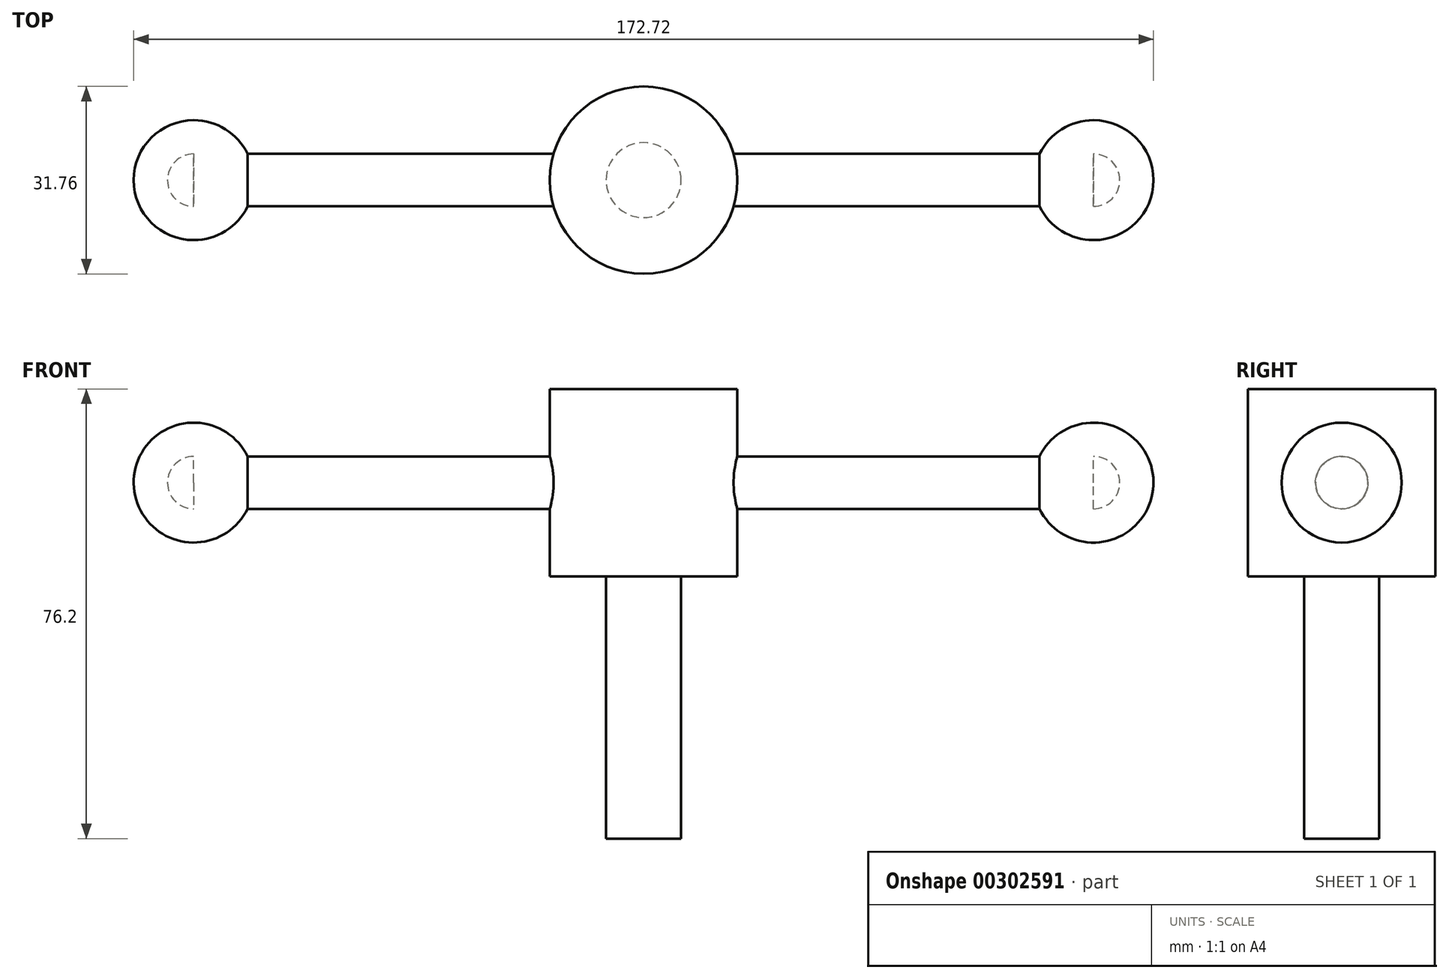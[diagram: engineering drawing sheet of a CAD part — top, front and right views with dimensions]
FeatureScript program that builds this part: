
annotation { "Feature Type Name" : "Feature", "Feature Type Description" : "" }
export const myFeature = defineFeature(function(context is Context, id is Id, definition is map)
    precondition{}
    {
        {
            var Q0;
            Q0=qCreatedBy(makeId("Top.planeOp"),FACE);
            var sketch = newSketch(context, id + "F0", { "sketchPlane" : qUnion([Q0])});
            skCircle(sketch, "E0", {"center": v(0, 0) * mm, "radius": 6.35 * mm});
            skSolve(sketch);
        }
        {
            var Q0;
            Q0 = qSketchRegion(id + "F0", true);
            extrude(context, id + "F1", {"entities" : qUnion([Q0]), "depth" : 76.2 * mm});
        }
        {
            var Q0;
            Q0=makeQuery(id+"F1.opExtrude","CAP_FACE",FACE,{"disambiguationData":[OSD([sQuery(id+"F0.wireOp",EDGE,"E0")])],"isStart":false});
            var sketch = newSketch(context, id + "F2", { "sketchPlane" : qUnion([Q0])});
            skCircle(sketch, "E1", {"center": v(0, 0) * mm, "radius": 15.88 * mm});
            skSolve(sketch);
        }
        {
            var Q0;
            Q0 = qSketchRegion(id + "F2", true);
            extrude(context, id + "F3", {"entities" : qUnion([Q0]), "operationType" : NewBodyOperationType.ADD, "oppositeDirection" : true, "depth" : 31.75 * mm});
        }
        {
            var Q0;
            Q0=qCreatedBy(makeId("Right.planeOp"),FACE);
            var sketch = newSketch(context, id + "F4", { "sketchPlane" : qUnion([Q0])});
            skLineSegment(sketch, "E2", {"start": v(0, 0) * mm, "end": v(0, 60.32) * mm});
            skCircle(sketch, "E3", {"center": v(0, 60.32) * mm, "radius": 4.45 * mm});
            skSolve(sketch);
        }
        {
            var Q0;
            Q0 = qSketchRegion(id + "F4", true);
            extrude(context, id + "F5", {"entities" : qUnion([Q0]), "operationType" : NewBodyOperationType.ADD, "endBound" : BoundingType.SYMMETRIC, "depth" : 152.4 * mm});
        }
        {
            var Q0;
            Q0=makeQuery(id+"F5.opExtrude","CAP_FACE",FACE,{"disambiguationData":[OSD([sQuery(id+"F4.wireOp",EDGE,"E3")])],"isStart":false});
            var sketch = newSketch(context, id + "F6", { "sketchPlane" : qUnion([Q0])});
            skArc(sketch, "E4", {"start": v(10.16, 60.32) * mm, "mid": v(0, 70.48) * mm, "end": v(-10.16, 60.32) * mm});
            skLineSegment(sketch, "E5", {"start": v(0, 60.32) * mm, "end": v(-10.16, 60.32) * mm});
            skLineSegment(sketch, "E6", {"start": v(0, 60.32) * mm, "end": v(10.16, 60.32) * mm});
            skSolve(sketch);
        }
        {
            var Q0;
            {var subQ0=sQuery(id+"F6.wireOp",EDGE,"E4");Q0=makeQuery(id+"F6.imprint","IMPRINT",FACE,{"disambiguationData":[TD([[makeQuery(id+"F6.imprint","IMPRINT",EDGE,{"derivedFrom":subQ0}),1.0]])]});}
            var Q1;
            Q1=sQuery(id+"F6.wireOp",EDGE,"E5");
            revolve(context, id + "F7", {"operationType" : NewBodyOperationType.ADD, "entities" : qUnion([Q0]), "axis" : qUnion([Q1]), "revolveType" : RevolveType.FULL});
        }
        {
            var Q0;
            Q0=makeQuery(id+"F5.opExtrude","CAP_FACE",FACE,{"disambiguationData":[OSD([sQuery(id+"F4.wireOp",EDGE,"E3")])],"isStart":true});
            var sketch = newSketch(context, id + "F8", { "sketchPlane" : qUnion([Q0])});
            skArc(sketch, "E7", {"start": v(10.16, 60.32) * mm, "mid": v(0, 70.48) * mm, "end": v(-10.16, 60.32) * mm});
            skLineSegment(sketch, "E8", {"start": v(-10.16, 60.32) * mm, "end": v(10.16, 60.32) * mm});
            skSolve(sketch);
        }
        {
            var Q0;
            {var subQ0=sQuery(id+"F8.wireOp",EDGE,"E7");Q0=makeQuery(id+"F8.imprint","IMPRINT",FACE,{"disambiguationData":[TD([[makeQuery(id+"F8.imprint","IMPRINT",EDGE,{"derivedFrom":subQ0}),1.0]])]});}
            var Q1;
            Q1=sQuery(id+"F8.wireOp",EDGE,"E8");
            revolve(context, id + "F9", {"operationType" : NewBodyOperationType.ADD, "entities" : qUnion([Q0]), "axis" : qUnion([Q1]), "revolveType" : RevolveType.FULL});
        }
    });
